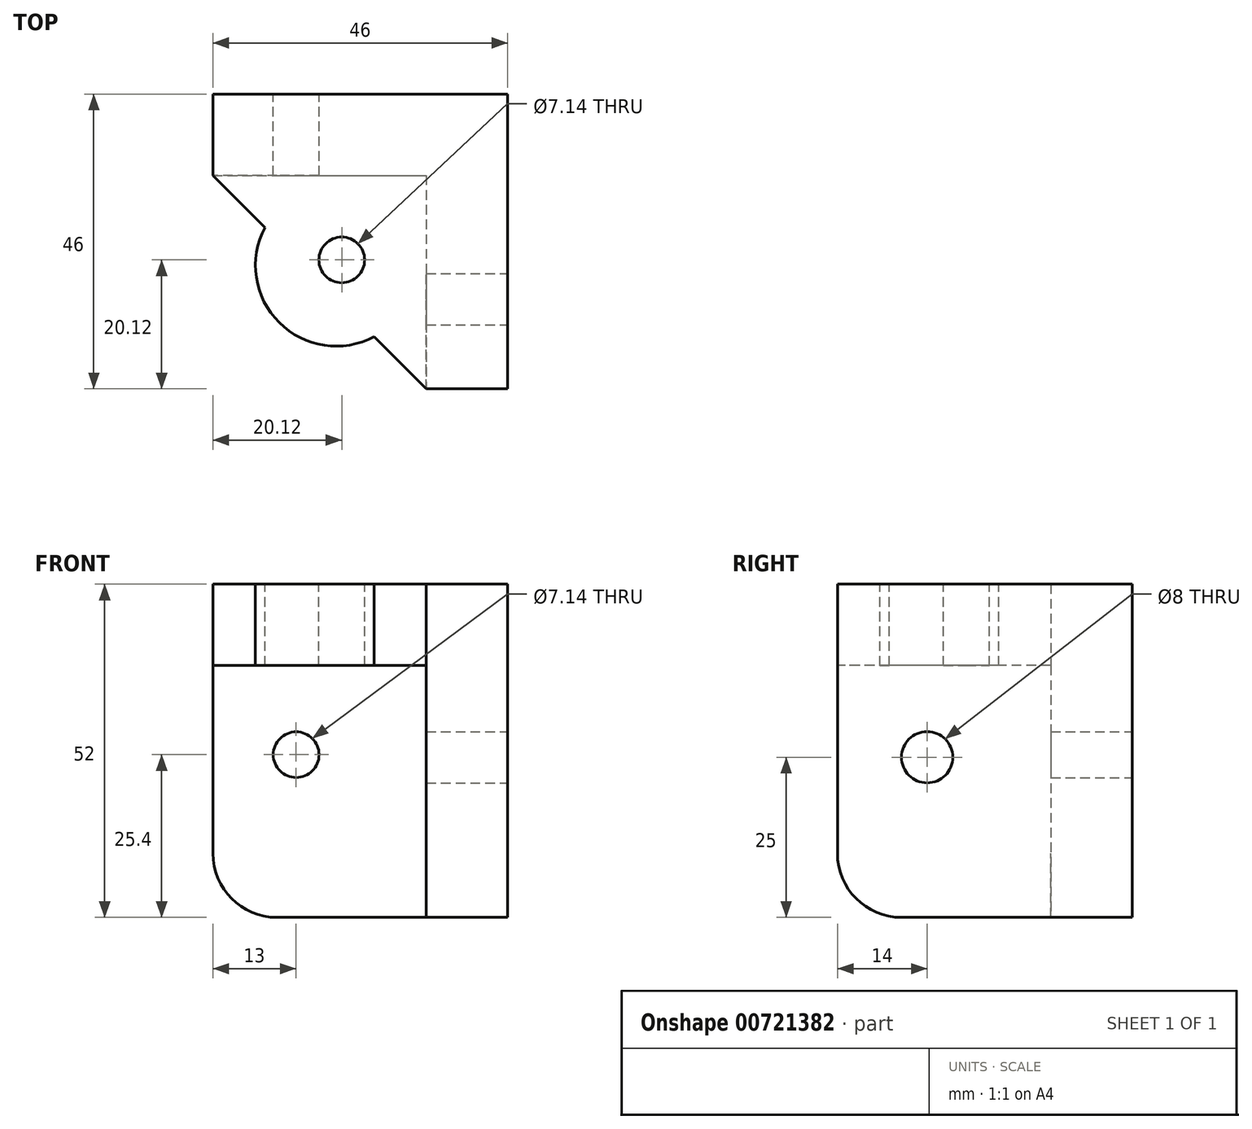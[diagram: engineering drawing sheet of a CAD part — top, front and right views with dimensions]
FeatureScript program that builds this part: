
annotation { "Feature Type Name" : "Feature", "Feature Type Description" : "" }
export const myFeature = defineFeature(function(context is Context, id is Id, definition is map)
    precondition{}
    {
        {
            var Q0;
            Q0=qCreatedBy(makeId("Top.planeOp"),FACE);
            var sketch = newSketch(context, id + "F0", { "sketchPlane" : qUnion([Q0])});
            skLineSegment(sketch, "E0.bottom", {"start": v(0, 0) * mm, "end": v(33.3, 0) * mm});
            skLineSegment(sketch, "E0.top", {"start": v(0, -12.7) * mm, "end": v(33.3, -12.7) * mm});
            skLineSegment(sketch, "E0.left", {"start": v(0, 0) * mm, "end": v(0, -12.7) * mm});
            skLineSegment(sketch, "E0.right", {"start": v(33.3, 0) * mm, "end": v(33.3, -12.7) * mm});
            skLineSegment(sketch, "E1.bottom", {"start": v(33.3, 0) * mm, "end": v(46, 0) * mm});
            skLineSegment(sketch, "E1.top", {"start": v(33.3, -46) * mm, "end": v(46, -46) * mm});
            skLineSegment(sketch, "E1.left", {"start": v(33.3, 0) * mm, "end": v(33.3, -46) * mm});
            skLineSegment(sketch, "E1.right", {"start": v(46, 0) * mm, "end": v(46, -46) * mm});
            skSolve(sketch);
        }
        {
            var Q0;
            Q0=qSketchRegion(id+"F0",true);
            extrude(context, id + "F1", {"entities" : qUnion([Q0]), "depth" : 52 * mm});
        }
        {
            var Q0;
            Q0=makeQuery(id+"F1.opExtrude","CAP_FACE",FACE,{"disambiguationData":[OSD([sQuery(id+"F0.wireOp",EDGE,"E0.bottom"),sQuery(id+"F0.wireOp",EDGE,"E0.top"),sQuery(id+"F0.wireOp",EDGE,"E0.left"),sQuery(id+"F0.wireOp",EDGE,"E1.bottom"),sQuery(id+"F0.wireOp",EDGE,"E1.top"),sQuery(id+"F0.wireOp",EDGE,"E1.left"),sQuery(id+"F0.wireOp",EDGE,"E1.right")])],"isStart":false});
            var sketch = newSketch(context, id + "F2", { "sketchPlane" : qUnion([Q0])});
            skLineSegment(sketch, "E2.bottom", {"start": v(46, 0) * mm, "end": v(0, 0) * mm});
            skLineSegment(sketch, "E2.top", {"start": v(46, -46) * mm, "end": v(0, -46) * mm, "construction": true});
            skLineSegment(sketch, "E2.left", {"start": v(46, 0) * mm, "end": v(46, -46) * mm});
            skLineSegment(sketch, "E2.right", {"start": v(0, 0) * mm, "end": v(0, -46) * mm, "construction": true});
            skLineSegment(sketch, "E3", {"start": v(0, 0) * mm, "end": v(0, -12.7) * mm});
            skLineSegment(sketch, "E4", {"start": v(0, -12.7) * mm, "end": v(33.3, -46) * mm});
            skLineSegment(sketch, "E5", {"start": v(33.3, -46) * mm, "end": v(46, -46) * mm});
            skArc(sketch, "E6", {"start": v(8.13, -20.83) * mm, "mid": v(10.34, -35.66) * mm, "end": v(25.17, -37.87) * mm});
            skLineSegment(sketch, "E7", {"start": v(46, 0) * mm, "end": v(16.65, -29.35) * mm, "construction": true});
            skSolve(sketch);
        }
        {
            var Q0;
            Q0=qSketchRegion(id+"F2",true);
            extrude(context, id + "F3", {"entities" : qUnion([Q0]), "operationType" : NewBodyOperationType.ADD, "oppositeDirection" : true, "depth" : 12.7 * mm});
        }
        {
            var Q0;
            Q0=makeQuery(id+"F1.opExtrude","SWEPT_FACE",FACE,{"disambiguationData":[OSD([sQuery(id+"F0.wireOp",EDGE,"E1.right")])]});
            var sketch = newSketch(context, id + "F4", { "sketchPlane" : qUnion([Q0])});
            skCircle(sketch, "E8", {"center": v(-32, 25) * mm, "radius": 4 * mm});
            skPoint(sketch, "E8.centerSnap0", {"position": v(-32, 0) * mm});
            skSolve(sketch);
        }
        {
            var Q0;
            Q0=qSketchRegion(id+"F4",true);
            extrude(context, id + "F5", {"entities" : qUnion([Q0]), "operationType" : NewBodyOperationType.REMOVE, "endBound" : BoundingType.THROUGH_ALL, "oppositeDirection" : true, "depth" : 25 * mm});
        }
        {
            var Q0;
            Q0=makeQuery(id+"F1.opExtrude","SWEPT_FACE",FACE,{"disambiguationData":[OSD([sQuery(id+"F0.wireOp",EDGE,"E0.bottom"),sQuery(id+"F0.wireOp",EDGE,"E1.bottom")])]});
            var sketch = newSketch(context, id + "F6", { "sketchPlane" : qUnion([Q0])});
            skCircle(sketch, "E9", {"center": v(-13, 25.4) * mm, "radius": 3.57 * mm});
            skSolve(sketch);
        }
        {
            var Q0;
            Q0=qSketchRegion(id+"F6",true);
            extrude(context, id + "F7", {"entities" : qUnion([Q0]), "operationType" : NewBodyOperationType.REMOVE, "oppositeDirection" : true, "depth" : 25 * mm});
        }
        {
            var Q0;
            Q0=makeQuery(id+"F3.boolean.opBoolean","MERGE",FACE,{"derivedFrom":[makeQuery(id+"F1.opExtrude","CAP_FACE",FACE,{"disambiguationData":[OSD([sQuery(id+"F0.wireOp",EDGE,"E0.bottom"),sQuery(id+"F0.wireOp",EDGE,"E0.top"),sQuery(id+"F0.wireOp",EDGE,"E0.left"),sQuery(id+"F0.wireOp",EDGE,"E1.bottom"),sQuery(id+"F0.wireOp",EDGE,"E1.top"),sQuery(id+"F0.wireOp",EDGE,"E1.left"),sQuery(id+"F0.wireOp",EDGE,"E1.right")])],"isStart":false}),makeQuery(id+"F3.opExtrude","CAP_FACE",FACE,{"disambiguationData":[OSD([sQuery(id+"F2.wireOp",EDGE,"E2.bottom"),sQuery(id+"F2.wireOp",EDGE,"E2.left"),sQuery(id+"F2.wireOp",EDGE,"E3"),sQuery(id+"F2.wireOp",EDGE,"E4"),sQuery(id+"F2.wireOp",EDGE,"E5"),sQuery(id+"F2.wireOp",EDGE,"E6")])],"isStart":true})]});
            var sketch = newSketch(context, id + "F8", { "sketchPlane" : qUnion([Q0])});
            skCircle(sketch, "E10", {"center": v(20.12, -25.88) * mm, "radius": 3.57 * mm});
            skLineSegment(sketch, "E11", {"start": v(46, 0) * mm, "end": v(10.34, -35.66) * mm, "construction": true});
            skSolve(sketch);
        }
        {
            var Q0;
            Q0=qSketchRegion(id+"F8",true);
            extrude(context, id + "F9", {"entities" : qUnion([Q0]), "operationType" : NewBodyOperationType.REMOVE, "oppositeDirection" : true, "depth" : 25 * mm});
        }
        {
            var Q0;
            Q0=makeQuery(id+"F1.opExtrude","CAP_EDGE",EDGE,{"disambiguationData":[OSD([sQuery(id+"F0.wireOp",EDGE,"E1.top")])],"isStart":true});
            var Q1;
            Q1=makeQuery(id+"F1.opExtrude","CAP_EDGE",EDGE,{"disambiguationData":[OSD([sQuery(id+"F0.wireOp",EDGE,"E0.left")])],"isStart":true});
            fillet(context, id + "F10", {"entities" : qUnion([Q0, Q1]), "radius" : 10 * mm, "tangentPropagation" : true, "allowEdgeOverflow" : false});
        }
    });
